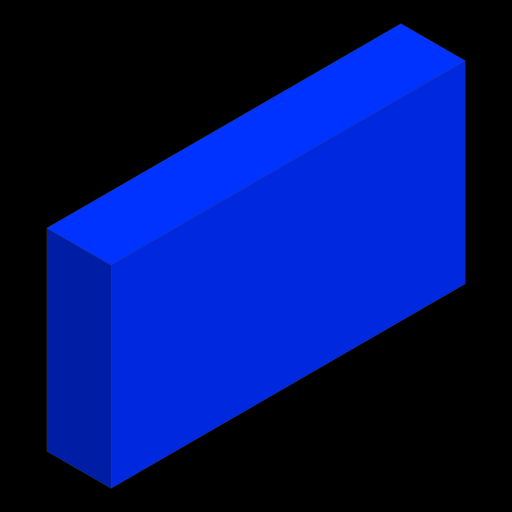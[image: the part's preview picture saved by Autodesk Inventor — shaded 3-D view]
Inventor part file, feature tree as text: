
AUTODESK INVENTOR PART (.ipt)
format: ipt  version: 2023 (Build 270158000, 158)  size: 93,184 bytes
history: native  units: mm
features: extrude x1, sketch x1
ambient origin geometry x8: Origin, YZ Plane, XZ Plane, XY Plane, X Axis, Y Axis, Z Axis, Center Point
bodies: Solid1 (feature_tree)
feature tree (2):
  extrude  "Extrusion1"  Depth=550.0mm
  sketch  "Sketch1"  dims[d0=100.0mm d1=550.0mm d2=300.0mm d3=0.0mm]
